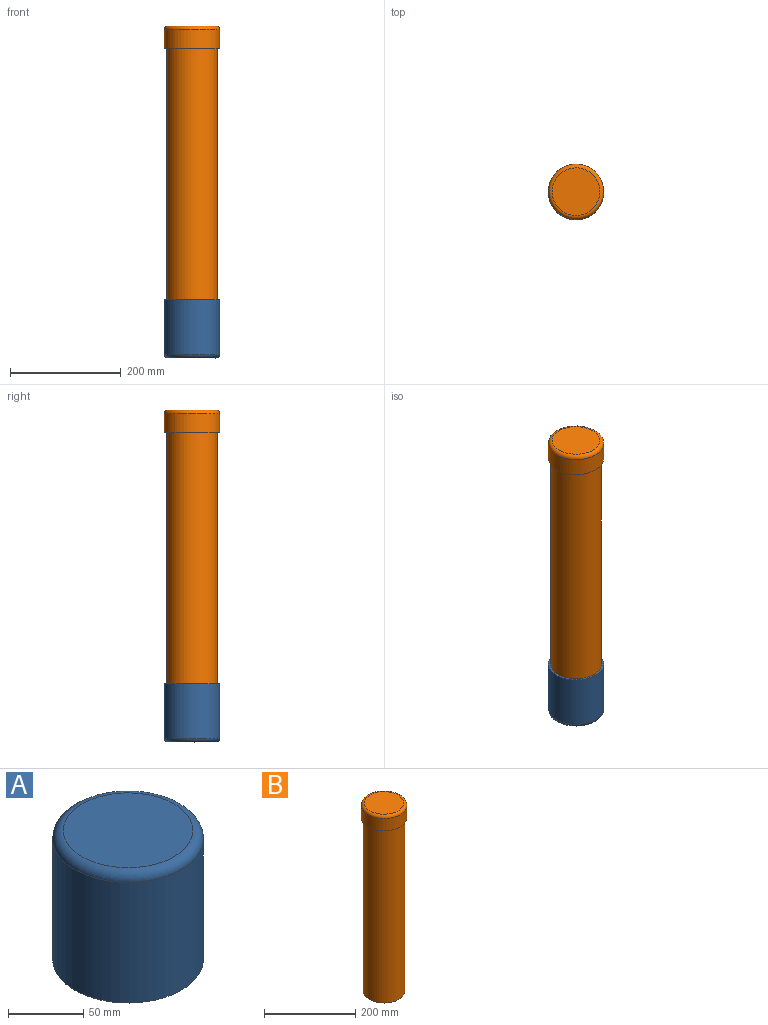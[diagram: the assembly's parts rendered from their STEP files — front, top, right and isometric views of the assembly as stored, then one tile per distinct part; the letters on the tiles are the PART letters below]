
ASSEMBLY  parts=2 mates=1
PART A: 8 faces, bbox 108.2x108.2x105 mm
  f0: cylinder r=42mm len=84mm, axis (0,0,1), area 13194.7mm2, adj f1,f2
  f1: plane 92x92mm, normal (0,0,-1), area 1105.8mm2, adj f0,f3
  f2: plane 84x84mm, normal (0,0,-1), area 5541.8mm2, adj f0
  f3: cylinder r=46mm len=92mm, axis (0,0,1), area 14451.3mm2, adj f1,f4
  f4: plane 100x100mm, normal (0,0,-1), area 1206.4mm2, adj f3,f6
  f5: plane 86x86mm, normal (0,0,1), area 5808.8mm2, adj f7
  f6: cylinder r=50mm len=100mm, axis (0,0,-1), area 30787.6mm2, adj f4,f7
  f7: torus R=43mm, axis (0,0,1), area 3278.6mm2, adj f5,f6
PART B: 8 faces, bbox 108.2x108.2x505 mm
  f0: cylinder r=42mm len=500mm, axis (0,0,1), area 131946.9mm2, adj f2,f3
  f1: cylinder r=46mm len=465mm, axis (0,0,1), area 134397.3mm2, adj f2,f4
  f2: plane 92x92mm, normal (0,0,-1), area 1105.8mm2, adj f0,f1
  f3: plane 84x84mm, normal (0,0,-1), area 5541.8mm2, adj f0
  f4: plane 100x100mm, normal (0,0,-1), area 1206.4mm2, adj f1,f6
  f5: plane 86x86mm, normal (0,0,1), area 5808.8mm2, adj f7
  f6: cylinder r=50mm len=100mm, axis (0,0,-1), area 10367.3mm2, adj f4,f7
  f7: torus R=43mm, axis (0,0,1), area 3278.6mm2, adj f5,f6
PLACE A rot(axis=(-1,0,0),180deg) t=(-236.66,-82.26,-568.26)mm
PLACE B t=(-236.66,-82.26,20.79)mm
MATE slider A.f0 <-> B.f0  axis (0,0,1) through (-236.66,-82.26,-517.26)mm
